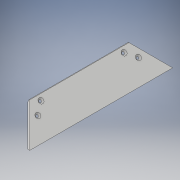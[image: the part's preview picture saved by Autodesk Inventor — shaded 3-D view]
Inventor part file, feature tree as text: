
AUTODESK INVENTOR PART (.ipt)
format: ipt  version: 2019 (Build 230136000, 136)  size: 128,512 bytes
history: native  units: mm
features: sketch x3, extrude x2, other x1, hole x1
ambient origin geometry x8: Origin, YZ Plane, XZ Plane, XY Plane, X Axis, Y Axis, Z Axis, Center Point
bodies: Body1 (feature_tree)
feature tree (7):
  other  "Bryła1"
  extrude  "Wyciągnięcie proste1"  Depth=30.0mm
  extrude  "Wyciągnięcie proste3"  TaperAngle=45.0deg  [1 undecoded]
  hole  "Otwór2"  [1 undecoded]
  sketch  "Szkic1"
  sketch  "Szkic4"
  sketch  "Szkic5"
note: 2 required parameter values undecoded (feature->parameter linkage not recoverable at this tier; creation-order binding heuristic only, values carry confidence <= 0.55)
